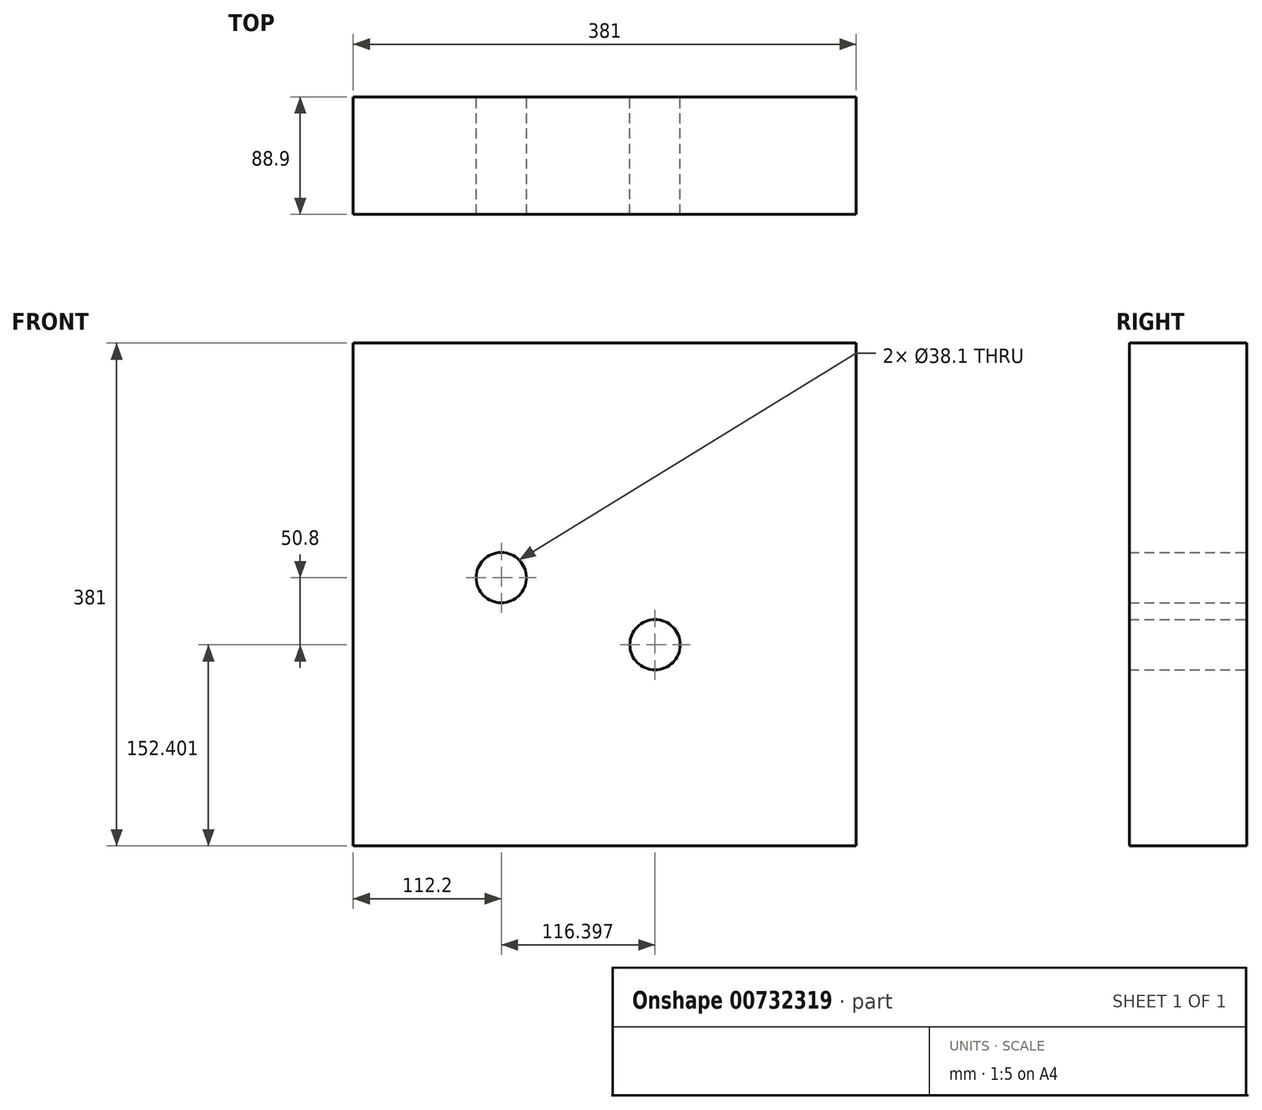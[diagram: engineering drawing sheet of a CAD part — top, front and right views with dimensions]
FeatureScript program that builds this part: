
annotation { "Feature Type Name" : "Feature", "Feature Type Description" : "" }
export const myFeature = defineFeature(function(context is Context, id is Id, definition is map)
    precondition{}
    {
        {
            var Q0;
            Q0=qCreatedBy(makeId("Front.planeOp"),FACE);
            var sketch = newSketch(context, id + "F0", { "sketchPlane" : qUnion([Q0])});
            skLineSegment(sketch, "E0.bottom", {"start": v(-321.44, 164.11) * mm, "end": v(59.56, 164.11) * mm});
            skLineSegment(sketch, "E0.top", {"start": v(-321.44, -216.89) * mm, "end": v(59.56, -216.89) * mm});
            skLineSegment(sketch, "E0.left", {"start": v(-321.44, 164.11) * mm, "end": v(-321.44, -216.89) * mm});
            skLineSegment(sketch, "E0.right", {"start": v(59.56, 164.11) * mm, "end": v(59.56, -216.89) * mm});
            skPoint(sketch, "E1", {"position": v(-209.24, -13.69) * mm});
            skPoint(sketch, "E2", {"position": v(-92.84, -64.49) * mm});
            skCircle(sketch, "E3", {"center": v(-209.24, -13.69) * mm, "radius": 19.05 * mm});
            skCircle(sketch, "E4", {"center": v(-92.84, -64.49) * mm, "radius": 19.05 * mm});
            skSolve(sketch);
        }
        {
            var Q0;
            Q0 = qSketchRegion(id + "F0", true);
            extrude(context, id + "F1", {"entities" : qUnion([Q0]), "depth" : 88.9 * mm, "offsetDistance" : 25.4 * mm});
        }
    });
